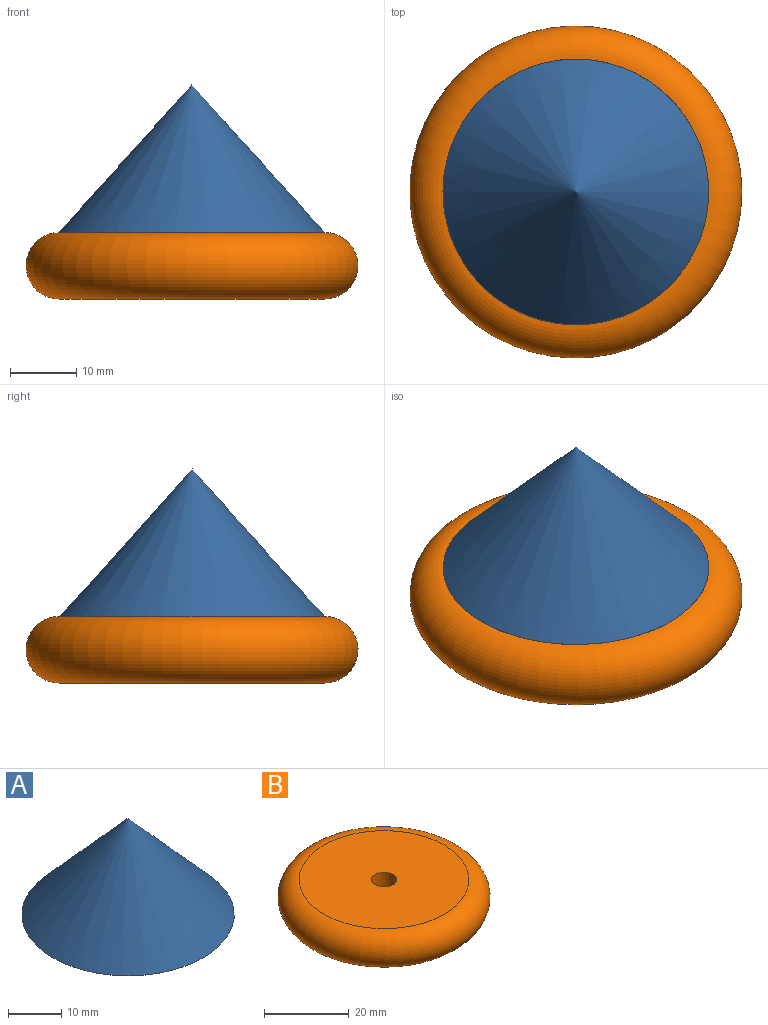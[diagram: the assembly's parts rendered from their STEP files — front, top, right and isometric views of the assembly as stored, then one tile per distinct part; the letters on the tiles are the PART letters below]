
ASSEMBLY  parts=2 mates=1
PART A: 2 faces, bbox 40x40x22.2 mm
  f0: plane 40x40mm, normal (0,0,-1), area 1256.6mm2, adj f1
  f1: cone r=20mm half-angle=42deg, axis (0,0,-1), area 1878mm2, adj f0
PART B: 4 faces, bbox 54.1x54.1x10 mm
  f0: plane 40x40mm, normal (0,0,1), area 1228.4mm2, adj f2,f3
  f1: plane 40x40mm, normal (0,0,-1), area 1228.4mm2, adj f2,f3
  f2: torus R=20mm, axis (0,0,1), area 2288.1mm2, adj f0,f1
  f3: cylinder r=3mm len=10mm, axis (0,0,-1), area 188.5mm2, adj f0,f1
PLACE A t=(-0.04,-0.06,4.94)mm
PLACE B t=(-0.04,-0.06,-5.06)mm
MATE planar A.f1 <-> B.f2  axis (0,0,-1) through (-0.04,-0.06,4.94)mm
